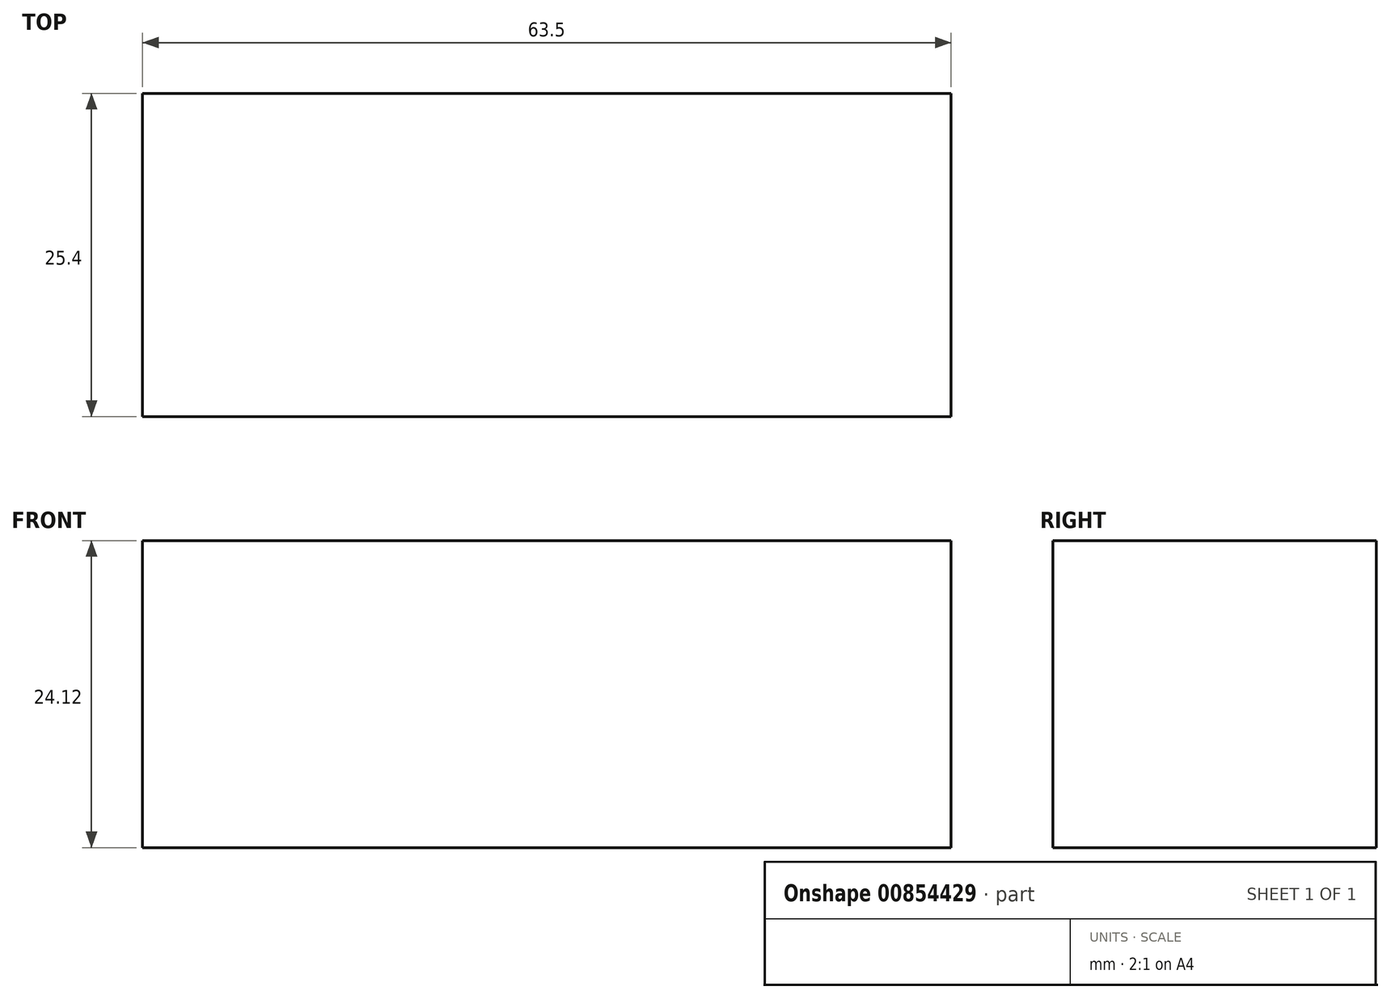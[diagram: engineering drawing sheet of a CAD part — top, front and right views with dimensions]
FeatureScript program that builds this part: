
annotation { "Feature Type Name" : "Feature", "Feature Type Description" : "" }
export const myFeature = defineFeature(function(context is Context, id is Id, definition is map)
    precondition{}
    {
        {
            var Q0;
            Q0=qCreatedBy(makeId("Front.planeOp"),FACE);
            var sketch = newSketch(context, id + "F0", { "sketchPlane" : qUnion([Q0])});
            skLineSegment(sketch, "E0.bottom", {"start": v(-31.75, 12.06) * mm, "end": v(31.75, 12.06) * mm});
            skLineSegment(sketch, "E0.top", {"start": v(-31.75, -12.06) * mm, "end": v(31.75, -12.06) * mm});
            skLineSegment(sketch, "E0.left", {"start": v(-31.75, 12.06) * mm, "end": v(-31.75, -12.06) * mm});
            skLineSegment(sketch, "E0.right", {"start": v(31.75, 12.06) * mm, "end": v(31.75, -12.06) * mm});
            skPoint(sketch, "E0.middle", {"position": v(0, 0) * mm});
            skSolve(sketch);
        }
        {
            var Q0;
            Q0 = qSketchRegion(id + "F0", true);
            extrude(context, id + "F1", {"entities" : qUnion([Q0]), "depth" : 25.4 * mm, "offsetDistance" : 25.4 * mm});
        }
    });
